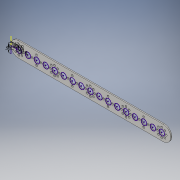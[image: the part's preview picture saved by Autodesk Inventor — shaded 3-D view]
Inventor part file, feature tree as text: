
AUTODESK INVENTOR PART (.ipt)
format: ipt  version: 2016 (Build 200138000, 138)  size: 232,448 bytes
history: native  units: in
note: dims shown in document units (in); Inventor stores cm internally (conversion verified against a paired STEP export)
features: sketch x4, extrude x2, hole x2, fillet x1, pattern_linear x1
ambient origin geometry x8: Origin, YZ Plane, XZ Plane, XY Plane, X Axis, Y Axis, Z Axis, Center Point
bodies: Solid1 (feature_tree)
feature tree (10):
  extrude  "Extrusion1"  Depth=1.0461in
  extrude  "Extrusion2"  Depth=0.0803in
  fillet  "Fillet1"  Radius=0.562in
  hole  "Hole1"  [1 undecoded]
  pattern_linear  "Rectangular Pattern1"  Count1=17 Spacing1=0.6193in
  hole  "Hole2"  [1 undecoded]
  sketch  "Sketch1"  dims[d0=11.0938in d1=1.0461in]
  sketch  "Sketch2"  dims[d2=0.0803in d3=0.0in d4=0.5023in d5=0.562in]
  sketch  "Sketch3"  dims[d6=0.0in d7=0.3839in]
  sketch  "Sketch4"  dims[d8=0.1in d11=6.6929in d13=0.6193in d14=0.3937in d16=1.0in d18=0.0803in d19=0.0in d20=0.52in d28=3.1496in d30=360.0deg d32=0.1378in d33=0.75in d34=0.375in d35=0.25in d36=0.5635in d37=1.0in d38=0.8108in d39=0.3096in d40=1.9685in d42=2.4772in d43=0.3096in d44=1.5748in d46=360.0deg d48=0.0in d49=0.6134in d50=1.5748in d52=2.4772in d53=0.3937in d55=1.0in d57=0.1378in d58=0.75in d59=0.375in d60=0.25in d61=0.5635in d62=1.0in d63=0.8108in]
note: 2 required parameter values undecoded (feature->parameter linkage not recoverable at this tier; creation-order binding heuristic only, values carry confidence <= 0.55)
